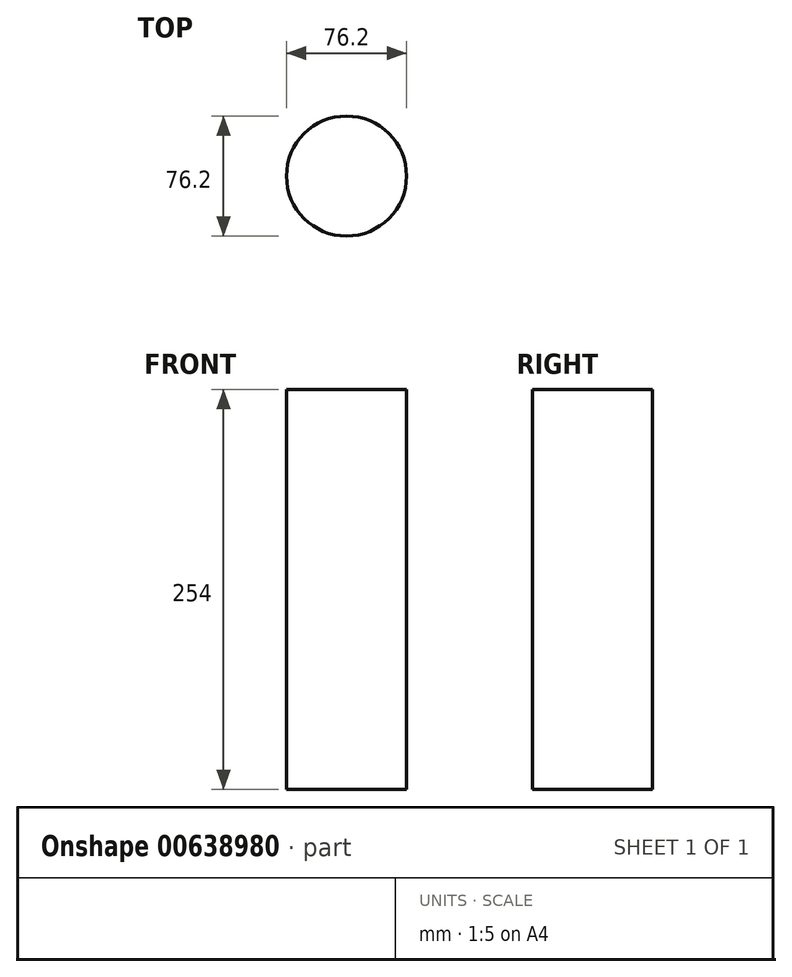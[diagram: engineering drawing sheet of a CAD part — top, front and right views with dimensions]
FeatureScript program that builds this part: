
annotation { "Feature Type Name" : "Feature", "Feature Type Description" : "" }
export const myFeature = defineFeature(function(context is Context, id is Id, definition is map)
    precondition{}
    {
        {
            var Q0;
            Q0=qCreatedBy(makeId("Top.planeOp"),FACE);
            var sketch = newSketch(context, id + "F0", { "sketchPlane" : qUnion([Q0])});
            skCircle(sketch, "E0", {"center": v(0, 0) * mm, "radius": 38.1 * mm});
            skSolve(sketch);
        }
        {
            var Q0;
            Q0=makeQuery(id+"F0.imprint","IMPRINT",FACE,{"disambiguationData":[TD([[makeQuery(id+"F0.imprint","IMPRINT",EDGE,{"derivedFrom":sQuery(id+"F0.wireOp",EDGE,"E0")}),1.0]])]});
            var sketch = newSketch(context, id + "F1", { "sketchPlane" : qUnion([Q0])});
            skCircle(sketch, "E1", {"center": v(0, 0) * mm, "radius": 25.4 * mm});
            skSolve(sketch);
        }
        {
            var Q0;
            Q0=qCreatedBy(makeId("Front.planeOp"),FACE);
            var sketch = newSketch(context, id + "F2", { "sketchPlane" : qUnion([Q0])});
            skSolve(sketch);
        }
        {
            var Q0;
            Q0 = qSketchRegion(id + "F2", true);
            var Q1;
            Q1=makeQuery(id+"F0.imprint","IMPRINT",FACE,{"disambiguationData":[TD([[makeQuery(id+"F0.imprint","IMPRINT",EDGE,{"derivedFrom":sQuery(id+"F0.wireOp",EDGE,"E0")}),1.0]])]});
            var Q2;
            Q2=makeQuery(id+"F1.imprint","IMPRINT",FACE,{"disambiguationData":[TD([[makeQuery(id+"F1.imprint","IMPRINT",EDGE,{"derivedFrom":sQuery(id+"F1.wireOp",EDGE,"E1")}),-1.0]])]});
            var Q3;
            Q3=makeQuery(id+"F1.imprint","IMPRINT",FACE,{"disambiguationData":[TD([[makeQuery(id+"F1.imprint","IMPRINT",EDGE,{"derivedFrom":sQuery(id+"F1.wireOp",EDGE,"E1")}),1.0]])]});
            extrude(context, id + "F3", {"entities" : qUnion([Q0, Q1, Q2, Q3]), "depth" : 254 * mm, "offsetDistance" : 25.4 * mm});
        }
    });
